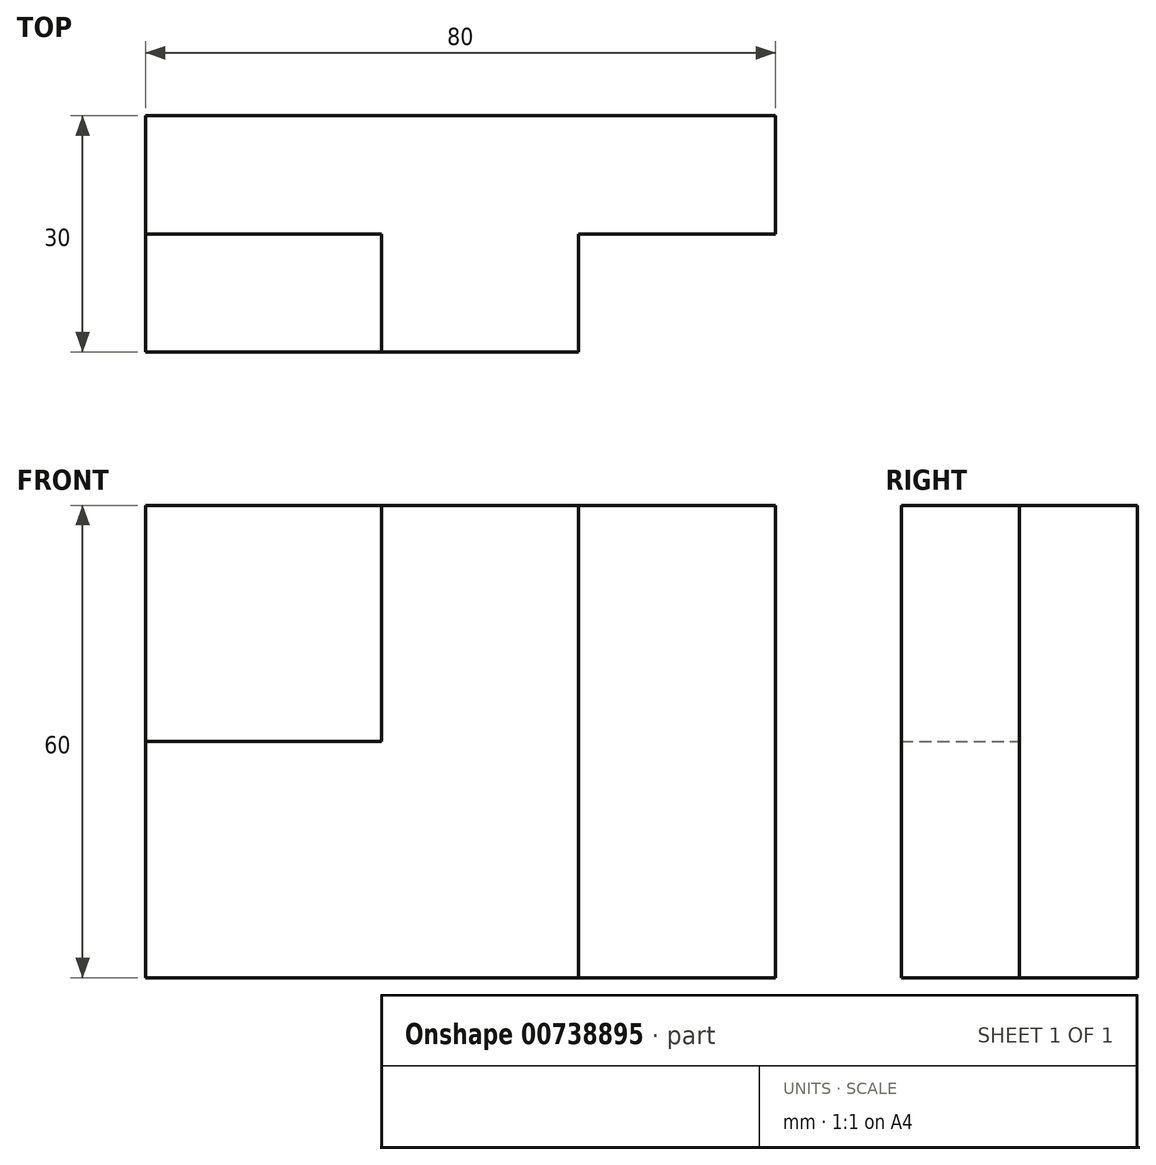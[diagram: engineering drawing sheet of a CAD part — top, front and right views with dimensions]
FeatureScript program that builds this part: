
annotation { "Feature Type Name" : "Feature", "Feature Type Description" : "" }
export const myFeature = defineFeature(function(context is Context, id is Id, definition is map)
    precondition{}
    {
        {
            var Q0;
            Q0=qCreatedBy(makeId("Front.planeOp"),FACE);
            var sketch = newSketch(context, id + "F0", { "sketchPlane" : qUnion([Q0])});
            skLineSegment(sketch, "E0.bottom", {"start": v(0, 0) * mm, "end": v(80, 0) * mm});
            skLineSegment(sketch, "E0.top", {"start": v(0, 60) * mm, "end": v(80, 60) * mm});
            skLineSegment(sketch, "E0.left", {"start": v(0, 0) * mm, "end": v(0, 60) * mm});
            skLineSegment(sketch, "E0.right", {"start": v(80, 0) * mm, "end": v(80, 60) * mm});
            skSolve(sketch);
        }
        {
            var Q0;
            Q0 = qSketchRegion(id + "F0", true);
            extrude(context, id + "F1", {"entities" : qUnion([Q0]), "depth" : 15 * mm, "offsetDistance" : 25 * mm});
        }
        {
            var Q0;
            Q0=makeQuery(id+"F1.opExtrude","CAP_FACE",FACE,{"disambiguationData":[OSD([sQuery(id+"F0.wireOp",EDGE,"E0.bottom"),sQuery(id+"F0.wireOp",EDGE,"E0.top"),sQuery(id+"F0.wireOp",EDGE,"E0.left"),sQuery(id+"F0.wireOp",EDGE,"E0.right")])],"isStart":false});
            var sketch = newSketch(context, id + "F2", { "sketchPlane" : qUnion([Q0])});
            skLineSegment(sketch, "E1", {"start": v(30, 60) * mm, "end": v(30, 30) * mm});
            skLineSegment(sketch, "E2", {"start": v(0, 30) * mm, "end": v(0, 0) * mm});
            skLineSegment(sketch, "E3", {"start": v(0, 0) * mm, "end": v(55, 0) * mm});
            skLineSegment(sketch, "E4", {"start": v(55, 0) * mm, "end": v(55, 60) * mm});
            skLineSegment(sketch, "E5", {"start": v(30, 30) * mm, "end": v(0, 30) * mm});
            skSolve(sketch);
        }
        {
            var Q0;
            Q0 = qSketchRegion(id + "F2", true);
            var Q1;
            {var subQ1=sQuery(id+"F2.wireOp",EDGE,"E1");Q1=makeQuery(id+"F2.imprint","IMPRINT",FACE,{"disambiguationData":[TD([[makeQuery(id+"F2.imprint","IMPRINT",EDGE,{"derivedFrom":subQ1}),1.0]])]});}
            extrude(context, id + "F3", {"entities" : qUnion([Q0, Q1]), "operationType" : NewBodyOperationType.ADD, "depth" : 15 * mm, "offsetDistance" : 25 * mm});
        }
    });
